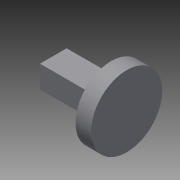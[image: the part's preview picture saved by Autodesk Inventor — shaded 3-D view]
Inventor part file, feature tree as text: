
AUTODESK INVENTOR PART (.ipt)
format: ipt  version: 2015 (Build 190159000, 159)  size: 84,480 bytes
history: native  units: in
note: dims shown in document units (in); Inventor stores cm internally (conversion verified against a paired STEP export)
features: extrude x2, sketch x2
ambient origin geometry x8: Origin, YZ Plane, XZ Plane, XY Plane, X Axis, Y Axis, Z Axis, Center Point
bodies: Solid1 (feature_tree)
feature tree (4):
  extrude  "Extrusion1"  Depth=0.2362in
  extrude  "Extrusion2"  Depth=0.2756in
  sketch  "Sketch1"  dims[d0=0.2362in d1=0.2362in]
  sketch  "Sketch2"  dims[d2=1.0236in d3=0.5118in d4=0.3937in d5=0.0in d6=1.2598in d7=0.2756in d8=0.0in]
